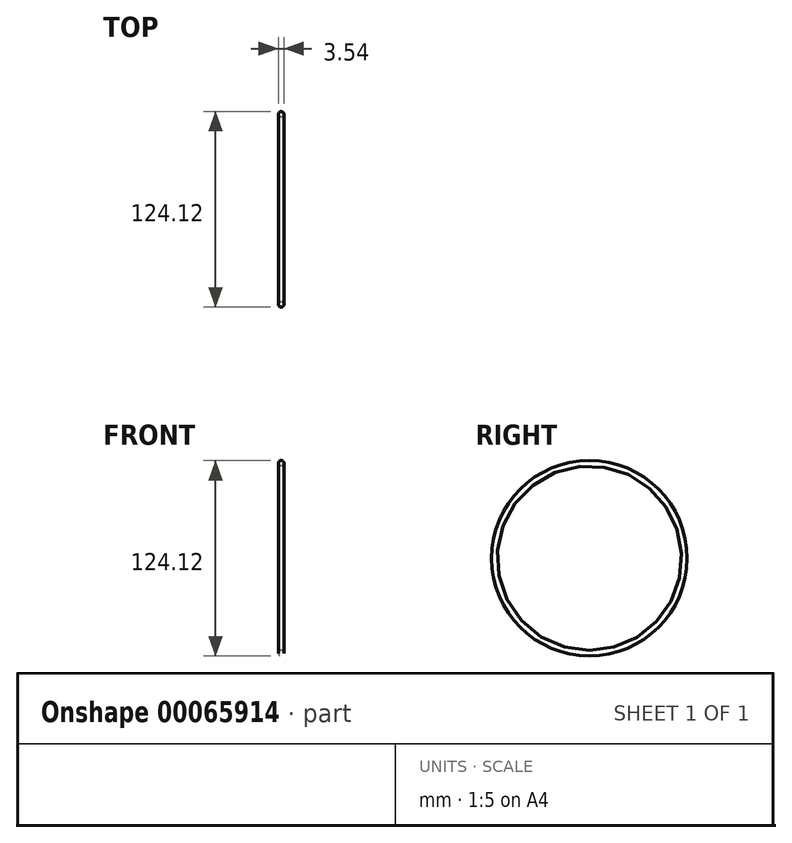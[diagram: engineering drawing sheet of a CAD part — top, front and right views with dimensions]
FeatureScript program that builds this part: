
annotation { "Feature Type Name" : "Feature", "Feature Type Description" : "" }
export const myFeature = defineFeature(function(context is Context, id is Id, definition is map)
    precondition{}
    {
        {
            var Q0;
            Q0=qCreatedBy(makeId("Front.planeOp"),FACE);
            var sketch = newSketch(context, id + "F0", { "sketchPlane" : qUnion([Q0])});
            skLineSegment(sketch, "E0", {"start": v(0, 0) * mm, "end": v(-6.06, 0) * mm, "construction": true});
            skCircle(sketch, "E1", {"center": v(0, 60.3) * mm, "radius": 1.77 * mm});
            skSolve(sketch);
        }
        {
            var Q0;
            Q0=makeQuery(id+"F0.imprint","IMPRINT",FACE,{"disambiguationData":[TD([[makeQuery(id+"F0.imprint","IMPRINT",EDGE,{"derivedFrom":sQuery(id+"F0.wireOp",EDGE,"E1")}),1.0]])]});
            var Q1;
            Q1=sQuery(id+"F0.wireOp",EDGE,"E0");
            revolve(context, id + "F1", {"entities" : qUnion([Q0]), "axis" : qUnion([Q1]), "revolveType" : RevolveType.FULL});
        }
    });
